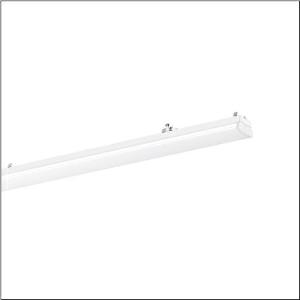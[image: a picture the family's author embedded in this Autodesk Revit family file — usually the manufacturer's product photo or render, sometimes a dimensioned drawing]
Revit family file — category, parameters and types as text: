
# Revit family: licross_r__21_recessed_opal_mo_52tl1ddv4e5g_bd2f
name_source: partatom
category: Lighting Fixtures
units: mm (PartAtom-declared; Revit-internal decimal feet)

## family parameters
Cut with Voids When Loaded = No
Host = Face
Light Source = No
Part Type = Normal
Room Calculation Point = No
Round Connector Dimension = Use Diameter
Shared = No

## types (1)
- --- (1 x LED, 14620 lm, 85.3 W, 4000K)
    Apparent Load = 85 VA
    CIE Flux Codes = 44 73 91 87 100
    Color Rendering = 80
    Color Temperature = 4000K
    Default Elevation = 1800 mm
    Description = Licross® 21 recessed opal MO, luminaire insert, of sheet steel, galvanised, coil coated, white, length: 2.250mm, width: 66mm, height: 67mm, LED rated luminous flux: 14.620lm, light colour: 840, control gear: DALI 2, with plug, 5-pole, with phase selection, mains connection: 220..240V, AC, 50/60Hz, rated input power: 85W, halogen-free wiring, primary optical cover: cover, of PMMA, light emission: direct with ceiling illumination distribution, primary light characteristic: symmetric, protection rating (complete): IP40, insulation class (complete): insulation class I (protective earthing), certification: CE, ENEC, VDE, UKCA, protection symbol: D if used in an environment without relevant dust loads with corresponding accessories, impact resistance: IK06, permissible ambient temperature for indoor applications: -25..+35°C, corresponds to IFS (International Featured Standards) requirements for safety and quality in the food industry, reducing of maximum allowable ambient temperature of 5°C with ceiling mounting, LABS conformity tested according to VDMA 24364:2018-05, packaging unit: 1 piece
    Height = 83 mm
    Lamp = 1 x LED
    Lamp Light Flux = 14620 lm
    Lamp Power = 85.3 W
    Lamp count = 1
    Length = 2250 mm
    Luminous efficacy = 171 lm/W
    Manufacturer = Siteco
    ModVariant = No
    Model = 52TL1DDV4E5G
    Mounting Place = Ceiling
    Mounting Type = Pendant
    Number of Poles = 1
    OnlyDefault = Yes
    Power Factor = 1
    Product Name = Licross® 21 recessed opal MO
    Product group = luminaire insert
    ProductGroupID = 901
    Protection Class = Protection class I
    Protection Degree = IP 40
    RLX_Detail_Level = 1
    RLX_Emergency_Light_Flux = 0 lm
    RLX_Emergency_Type = 0
    RLX_Emergency_Type_DB = No
    RlxData = <blob elided: 27037 chars, md5=c8fef8ac>
    Socket = socket
    Standby Power = 0 W
    System Light Flux = 14620 lm
    System Power = 85 W
    Type Comments = factory setting: luminous flux: 100 % | dim-lin: 254 | 390 mA
    Type Image = l_1313666.jpg
    URL = http://relux.com
    VarID = @adj_023467
    Voltage = 0 V
    Weight = 0.00 kg
    Width = 76 mm

## geometry (parser evidence)
native form markers: Blend x4, Sweep x13
no freeform markers — native parametric forms only
